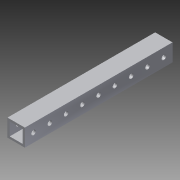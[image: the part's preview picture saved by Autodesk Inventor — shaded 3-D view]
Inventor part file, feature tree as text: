
AUTODESK INVENTOR PART (.ipt)
format: ipt  version: 2013 (Build 170138000, 138)  size: 114,688 bytes
history: native  units: in
note: dims shown in document units (in); Inventor stores cm internally (conversion verified against a paired STEP export)
features: extrude x2, sketch x1
ambient origin geometry x8: Origin, YZ Plane, XZ Plane, XY Plane, X Axis, Y Axis, Z Axis, Center Point
bodies: Solid1 (feature_tree)
feature tree (3):
  extrude  "Extrusion1"  Depth=1.0in
  extrude  "Extrusion2"  Depth=0.125in
  sketch  "Sketch1"  dims[d0=1.0in d1=1.0in d2=0.125in d3=8.5in d4=0.0in d5=0.5in d7=0.26in d8=16.5in d9=0.0in d13=8.5in d14=3.5433in d16=0.9375in d17=0.3937in d19=1.0in]
